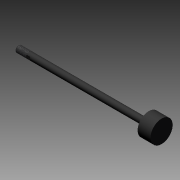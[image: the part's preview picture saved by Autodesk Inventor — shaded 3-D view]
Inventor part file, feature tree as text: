
AUTODESK INVENTOR PART (.ipt)
format: ipt  version: 2014 (Build 180170000, 170)  size: 162,304 bytes
history: native  units: in
note: dims shown in document units (in); Inventor stores cm internally (conversion verified against a paired STEP export)
features: other x98, sketch x3, revolve x2, thread x1, extrude x1
ambient origin geometry x8: Origin, YZ Plane, XZ Plane, XY Plane, X Axis, Y Axis, Z Axis, Center Point
bodies: Solid1 (feature_tree)
feature tree (105):
  revolve  "Revolution1"  Angle=360.0deg
  revolve  "Revolution2"  [1 undecoded]
  thread  "Thread1"  [1 undecoded]
  extrude  "Extrusion1"  [1 undecoded]
  other  "dia1_XY"
  other  "dia1_YZ"
  other  "dia1_ZX"
  other  "dia1_X"
  other  "dia1_Y"
  other  "dia1_Z"
  other  "dia1_Center"
  other  "dia12_XY"
  other  "dia12_YZ"
  other  "dia12_ZX"
  other  "dia12_X"
  other  "dia12_Y"
  other  "dia12_Z"
  other  "dia12_Center"
  other  "dia2_XY"
  other  "dia2_YZ"
  other  "dia2_ZX"
  other  "dia2_X"
  other  "dia2_Y"
  other  "dia2_Z"
  other  "dia2_Center"
  other  "dia22_XY"
  other  "dia22_YZ"
  other  "dia22_ZX"
  other  "dia22_X"
  other  "dia22_Y"
  other  "dia22_Z"
  other  "dia22_Center"
  other  "rl1_XY"
  other  "rl1_YZ"
  other  "rl1_ZX"
  other  "rl1_X"
  other  "rl1_Y"
  other  "rl1_Z"
  other  "rl1_Center"
  other  "rl2_XY"
  other  "rl2_YZ"
  other  "rl2_ZX"
  other  "rl2_X"
  other  "rl2_Y"
  other  "rl2_Z"
  other  "rl2_Center"
  other  "rod_cp_XY"
  other  "rod_cp_YZ"
  other  "rod_cp_ZX"
  other  "rod_cp_X"
  other  "rod_cp_Y"
  other  "rod_cp_Z"
  other  "rod_cp_Center"
  other  "thd1_XY"
  other  "thd1_YZ"
  other  "thd1_ZX"
  other  "thd1_X"
  other  "thd1_Y"
  other  "thd1_Z"
  other  "thd1_Center"
  other  "thd2_XY"
  other  "thd2_YZ"
  other  "thd2_ZX"
  other  "thd2_X"
  other  "thd2_Y"
  other  "thd2_Z"
  other  "thd2_Center"
  other  "to_rod_clevis_XY"
  other  "to_rod_clevis_YZ"
  other  "to_rod_clevis_ZX"
  other  "to_rod_clevis_X"
  other  "to_rod_clevis_Y"
  other  "to_rod_clevis_Z"
  other  "to_rod_clevis_Center"
  other  "wf1_XY"
  other  "wf1_YZ"
  other  "wf1_ZX"
  other  "wf1_X"
  other  "wf1_Y"
  other  "wf1_Z"
  other  "wf1_Center"
  other  "wf2_XY"
  other  "wf2_YZ"
  other  "wf2_ZX"
  other  "wf2_X"
  other  "wf2_Y"
  other  "wf2_Z"
  other  "wf2_Center"
  other  "wfw1_XY"
  other  "wfw1_YZ"
  other  "wfw1_ZX"
  other  "wfw1_X"
  other  "wfw1_Y"
  other  "wfw1_Z"
  other  "wfw1_Center"
  other  "wfw2_XY"
  other  "wfw2_YZ"
  other  "wfw2_ZX"
  other  "wfw2_X"
  other  "wfw2_Y"
  other  "wfw2_Z"
  other  "wfw2_Center"
  sketch  "Sketch_1"  dims[d0=360.0deg d1=360.0deg]
  sketch  "Sketch_3"  dims[d2=0.7203in d3=0.0in d4=0.25in d5=0.0in]
  sketch  "Sketch_10"
note: 3 required parameter values undecoded (feature->parameter linkage not recoverable at this tier; creation-order binding heuristic only, values carry confidence <= 0.55)